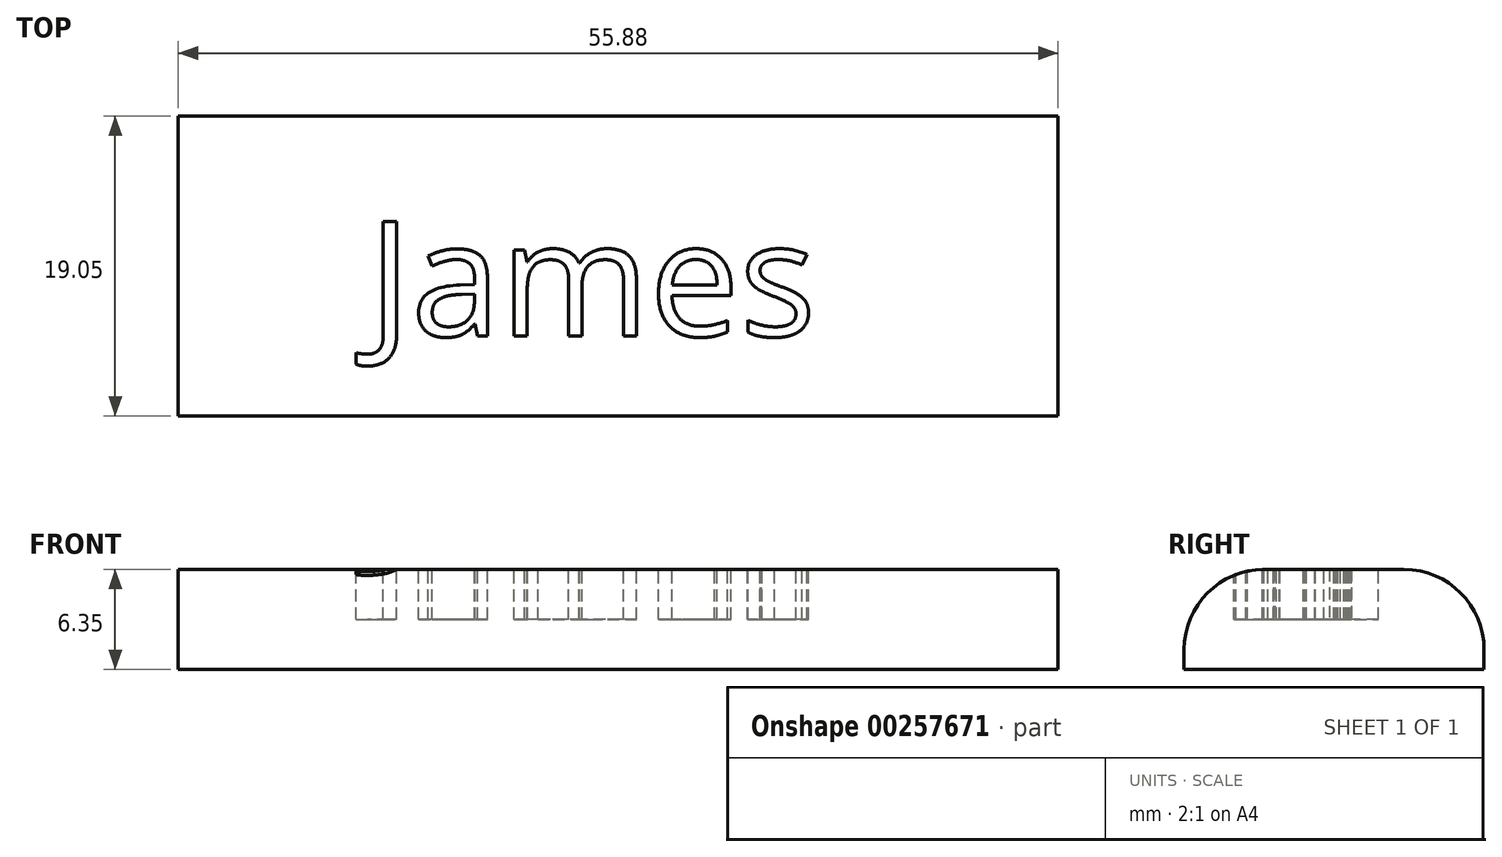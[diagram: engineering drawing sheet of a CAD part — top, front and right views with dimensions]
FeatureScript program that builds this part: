
annotation { "Feature Type Name" : "Feature", "Feature Type Description" : "" }
export const myFeature = defineFeature(function(context is Context, id is Id, definition is map)
    precondition{}
    {
        {
            var Q0;
            Q0=qCreatedBy(makeId("Top.planeOp"),FACE);
            var sketch = newSketch(context, id + "F0", { "sketchPlane" : qUnion([Q0])});
            skLineSegment(sketch, "E0.bottom", {"start": v(-69.82, 52) * mm, "end": v(-13.94, 52) * mm});
            skLineSegment(sketch, "E0.top", {"start": v(-69.82, 32.94) * mm, "end": v(-13.94, 32.94) * mm});
            skLineSegment(sketch, "E0.left", {"start": v(-69.82, 52) * mm, "end": v(-69.82, 32.94) * mm});
            skLineSegment(sketch, "E0.right", {"start": v(-13.94, 52) * mm, "end": v(-13.94, 32.94) * mm});
            skSolve(sketch);
        }
        {
            var Q0;
            Q0 = qSketchRegion(id + "F0", true);
            extrude(context, id + "F1", {"entities" : qUnion([Q0]), "depth" : 6.35 * mm});
        }
        {
            var Q0;
            Q0=makeQuery(id+"F1.opExtrude","CAP_EDGE",EDGE,{"disambiguationData":[OSD([sQuery(id+"F0.wireOp",EDGE,"E0.bottom")])],"isStart":false});
            fillet(context, id + "F2", {"entities" : qUnion([Q0]), "radius" : 5.08 * mm, "tangentPropagation" : true, "allowEdgeOverflow" : false});
        }
        {
            var Q0;
            Q0=makeQuery(id+"F1.opExtrude","CAP_EDGE",EDGE,{"disambiguationData":[OSD([sQuery(id+"F0.wireOp",EDGE,"E0.top")])],"isStart":false});
            fillet(context, id + "F3", {"entities" : qUnion([Q0]), "radius" : 5.08 * mm, "tangentPropagation" : true, "allowEdgeOverflow" : false});
        }
        {
            var Q0;
            Q0=makeQuery(id+"F1.opExtrude","CAP_FACE",FACE,{"disambiguationData":[OSD([sQuery(id+"F0.wireOp",EDGE,"E0.bottom"),sQuery(id+"F0.wireOp",EDGE,"E0.top"),sQuery(id+"F0.wireOp",EDGE,"E0.left"),sQuery(id+"F0.wireOp",EDGE,"E0.right")])],"isStart":false});
            var sketch = newSketch(context, id + "F4", { "sketchPlane" : qUnion([Q0])});
            skText(sketch, "E1", { "text": "James", "fontName": "OpenSans-Regular.ttf"});
            const initialGuessF4  = {"E1": [-0.05774, 0.03802, 1, 0, 0.00733]};
            skSetInitialGuess(sketch, initialGuessF4);
            skSolve(sketch);
        }
        {
            var Q0;
            Q0 = qSketchRegion(id + "F4", true);
            extrude(context, id + "F5", {"entities" : qUnion([Q0]), "operationType" : NewBodyOperationType.REMOVE, "oppositeDirection" : true, "depth" : 3.17 * mm});
        }
        {
            var Q0;
            Q0 = qSketchRegion(id + "F4", true);
            extrude(context, id + "F6", {"entities" : qUnion([Q0]), "operationType" : NewBodyOperationType.REMOVE, "oppositeDirection" : true, "depth" : 3.17 * mm});
        }
    });
